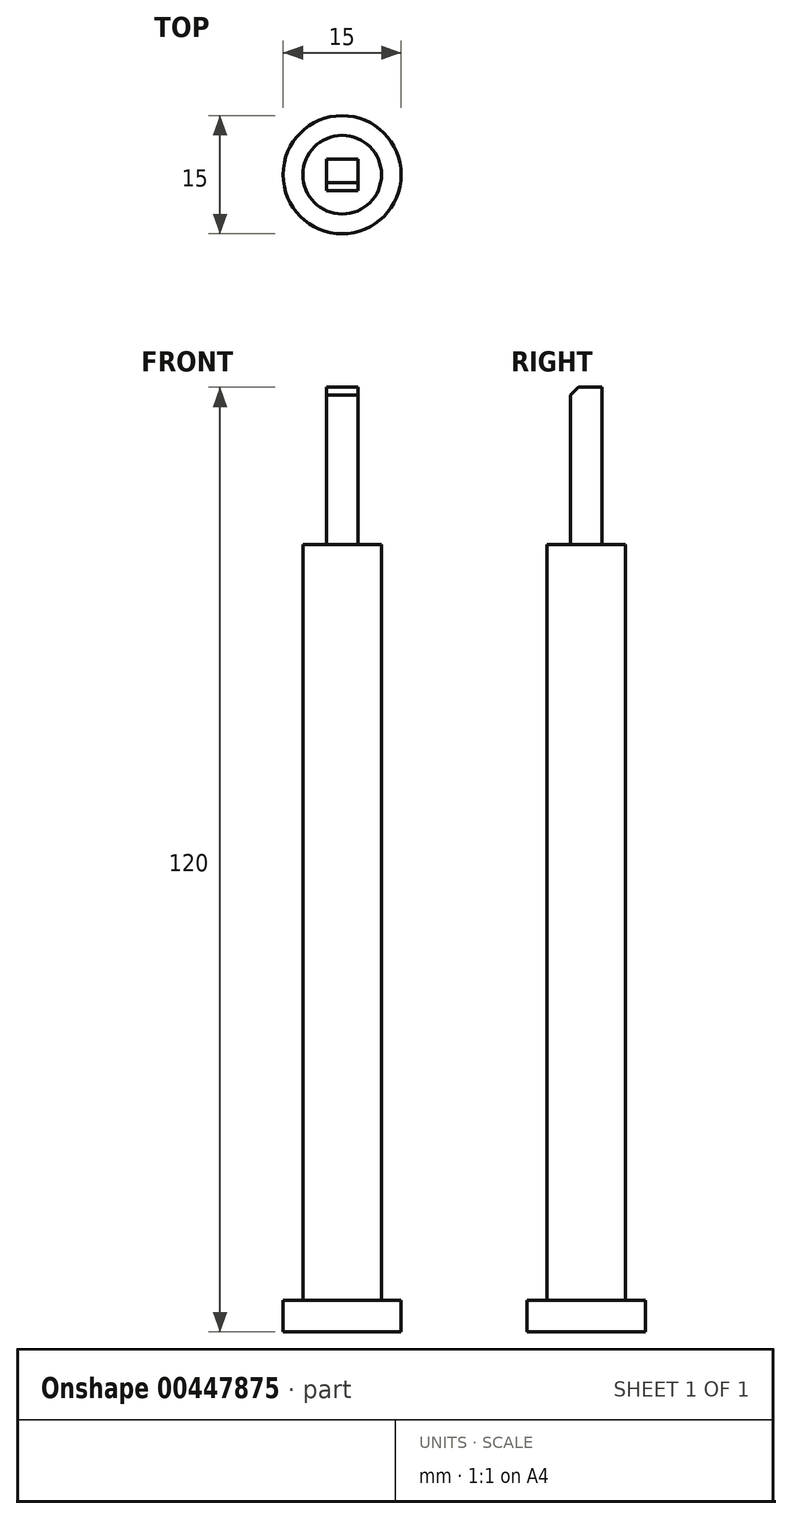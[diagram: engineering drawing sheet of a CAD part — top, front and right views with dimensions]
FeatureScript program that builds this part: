
annotation { "Feature Type Name" : "Feature", "Feature Type Description" : "" }
export const myFeature = defineFeature(function(context is Context, id is Id, definition is map)
    precondition{}
    {
        {
            var Q0;
            Q0=qCreatedBy(makeId("Top.planeOp"),FACE);
            var sketch = newSketch(context, id + "F0", { "sketchPlane" : qUnion([Q0])});
            skCircle(sketch, "E0", {"center": v(0, 0) * mm, "radius": 7.5 * mm});
            skSolve(sketch);
        }
        {
            var Q0;
            Q0=qSketchRegion(id+"F0",true);
            extrude(context, id + "F1", {"entities" : qUnion([Q0]), "depth" : 4 * mm});
        }
        {
            var Q0;
            Q0=qCreatedBy(makeId("Top.planeOp"),FACE);
            var sketch = newSketch(context, id + "F2", { "sketchPlane" : qUnion([Q0])});
            skCircle(sketch, "E1", {"center": v(0, 0) * mm, "radius": 5 * mm});
            skSolve(sketch);
        }
        {
            var Q0;
            Q0=qSketchRegion(id+"F2",true);
            extrude(context, id + "F3", {"entities" : qUnion([Q0]), "operationType" : NewBodyOperationType.ADD, "depth" : 100 * mm});
        }
        {
            var Q0;
            Q0=makeQuery(id+"F3.opExtrude","CAP_FACE",FACE,{"disambiguationData":[OSD([sQuery(id+"F2.wireOp",EDGE,"E1")])],"isStart":false});
            var sketch = newSketch(context, id + "F4", { "sketchPlane" : qUnion([Q0])});
            skLineSegment(sketch, "E2.bottom", {"start": v(-2, 2) * mm, "end": v(2, 2) * mm});
            skLineSegment(sketch, "E2.top", {"start": v(-2, -2) * mm, "end": v(2, -2) * mm});
            skLineSegment(sketch, "E2.left", {"start": v(-2, 2) * mm, "end": v(-2, -2) * mm});
            skLineSegment(sketch, "E2.right", {"start": v(2, 2) * mm, "end": v(2, -2) * mm});
            skSolve(sketch);
        }
        {
            var Q0;
            Q0=makeQuery(id+"F4.imprint","IMPRINT",FACE,{"disambiguationData":[TD([[makeQuery(id+"F4.imprint","IMPRINT",EDGE,{"derivedFrom":sQuery(id+"F4.wireOp",EDGE,"E2.bottom")}),-1.0]])]});
            extrude(context, id + "F5", {"entities" : qUnion([Q0]), "operationType" : NewBodyOperationType.ADD, "depth" : 20 * mm});
        }
        {
            var Q0;
            Q0=qCreatedBy(makeId("Right.planeOp"),FACE);
            var sketch = newSketch(context, id + "F6", { "sketchPlane" : qUnion([Q0])});
            skLineSegment(sketch, "E3", {"start": v(-3, 121) * mm, "end": v(-3, 118) * mm});
            skLineSegment(sketch, "E4", {"start": v(-3, 118) * mm, "end": v(0, 121) * mm});
            skLineSegment(sketch, "E5", {"start": v(0, 121) * mm, "end": v(-3, 121) * mm});
            skSolve(sketch);
        }
        {
            var Q0;
            Q0=makeQuery(id+"F6.imprint","IMPRINT",FACE,{"disambiguationData":[TD([[makeQuery(id+"F6.imprint","IMPRINT",EDGE,{"derivedFrom":sQuery(id+"F6.wireOp",EDGE,"E3")}),1.0]])]});
            extrude(context, id + "F7", {"entities" : qUnion([Q0]), "operationType" : NewBodyOperationType.REMOVE, "oppositeDirection" : true, "depth" : 25 * mm, "hasSecondDirection" : true, "secondDirectionOppositeDirection" : false, "secondDirectionDepth" : 25 * mm});
        }
    });
